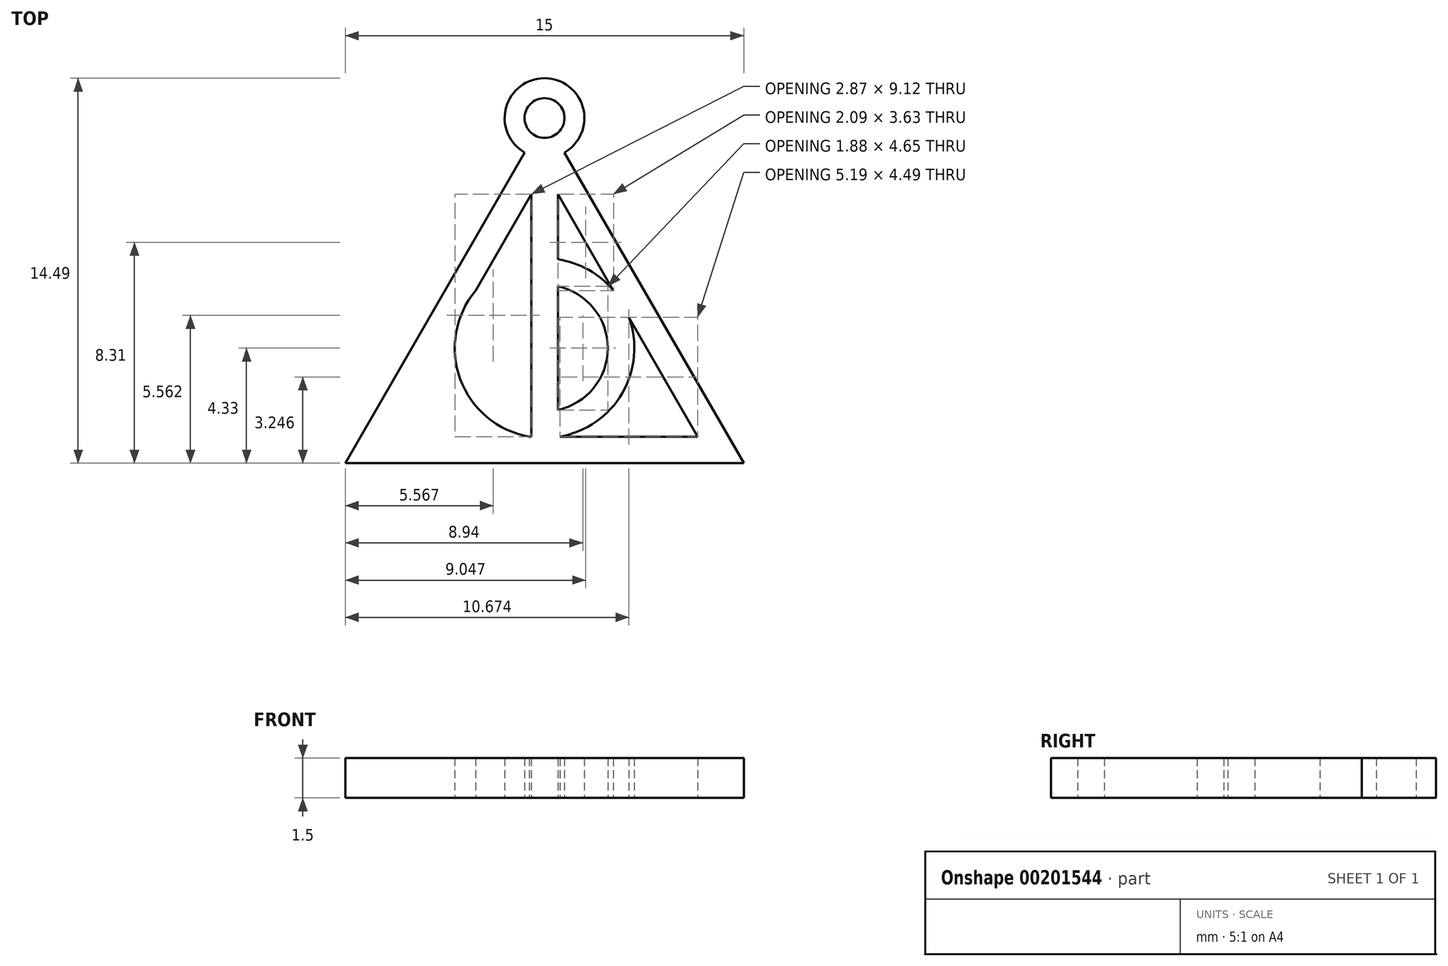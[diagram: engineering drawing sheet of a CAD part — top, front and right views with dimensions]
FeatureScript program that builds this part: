
annotation { "Feature Type Name" : "Feature", "Feature Type Description" : "" }
export const myFeature = defineFeature(function(context is Context, id is Id, definition is map)
    precondition{}
    {
        {
            var Q0;
            Q0=qCreatedBy(makeId("Top.planeOp"),FACE);
            var sketch = newSketch(context, id + "F0", { "sketchPlane" : qUnion([Q0])});
            skLineSegment(sketch, "E0", {"start": v(0, 0) * mm, "end": v(-7.5, -13) * mm});
            skLineSegment(sketch, "E1", {"start": v(-7.5, -13) * mm, "end": v(7.5, -13) * mm});
            skLineSegment(sketch, "E2", {"start": v(7.5, -13) * mm, "end": v(0, 0) * mm});
            skCircle(sketch, "E3", {"center": v(0, 0) * mm, "radius": 1.5 * mm});
            skCircle(sketch, "E4", {"center": v(0, 0) * mm, "radius": 0.75 * mm});
            skLineSegment(sketch, "E5.0", {"start": v(0, -2) * mm, "end": v(-5.77, -12) * mm});
            skLineSegment(sketch, "E5.1", {"start": v(5.77, -12) * mm, "end": v(0, -2) * mm});
            skLineSegment(sketch, "E5.2", {"start": v(-5.77, -12) * mm, "end": v(5.77, -12) * mm});
            skLineSegment(sketch, "E6", {"start": v(0, 0) * mm, "end": v(0, -13) * mm, "construction": true});
            skLineSegment(sketch, "E7", {"start": v(-0.5, -2.87) * mm, "end": v(-0.5, -12) * mm});
            skLineSegment(sketch, "E8.MirrorCS", {"start": v(0.5, -2.87) * mm, "end": v(0.5, -12) * mm});
            skCircle(sketch, "E9", {"center": v(0, -8.66) * mm, "radius": 3.38 * mm});
            skLineSegment(sketch, "E10", {"start": v(0, -8.66) * mm, "end": v(-2.93, -6.97) * mm, "construction": true});
            skPoint(sketch, "E11", {"position": v(0, -12.04) * mm});
            skCircle(sketch, "E12.0", {"center": v(0, -8.66) * mm, "radius": 2.38 * mm});
            skSolve(sketch);
        }
        {
            var Q0;
            {var subQ0=sQuery(id+"F0.wireOp",EDGE,"E3");var subQ1=sQuery(id+"F0.wireOp",EDGE,"E0");var subQ2=makeQuery(id+"F0.imprint","INTERSECT",VERTEX,{"derivedFrom":[subQ1,subQ0]});Q0=makeQuery(id+"F0.imprint","IMPRINT",FACE,{"disambiguationData":[TD([[makeQuery(id+"F0.imprint","IMPRINT",EDGE,{"disambiguationData":[TD([[subQ2,1.0]])],"derivedFrom":subQ1}),-1.0]])]});}
            var Q1;
            {var subQ0=sQuery(id+"F0.wireOp",EDGE,"E3");var subQ1=sQuery(id+"F0.wireOp",EDGE,"E0");var subQ2=makeQuery(id+"F0.imprint","INTERSECT",VERTEX,{"derivedFrom":[subQ1,subQ0]});Q1=makeQuery(id+"F0.imprint","IMPRINT",FACE,{"disambiguationData":[TD([[makeQuery(id+"F0.imprint","IMPRINT",EDGE,{"disambiguationData":[TD([[subQ2,1.0]])],"derivedFrom":subQ1}),1.0]])]});}
            var Q2;
            {var subQ1=sQuery(id+"F0.wireOp",EDGE,"E5.1");var subQ5=sQuery(id+"F0.wireOp",EDGE,"E5.0");var subQ6=makeQuery(id+"F0.imprint","INTERSECT",VERTEX,{"derivedFrom":[subQ5,subQ1]});Q2=makeQuery(id+"F0.imprint","IMPRINT",FACE,{"disambiguationData":[TD([[makeQuery(id+"F0.imprint","IMPRINT",EDGE,{"disambiguationData":[TD([[subQ6,-1.0]])],"derivedFrom":subQ5}),1.0]])]});}
            var Q3;
            {var subQ0=sQuery(id+"F0.wireOp",EDGE,"E12.0");var subQ1=sQuery(id+"F0.wireOp",EDGE,"E7");var subQ2=makeQuery(id+"F0.imprint","INTERSECT",VERTEX,{"disambiguationData":[OD(0.0)],"derivedFrom":[subQ1,subQ0]});Q3=makeQuery(id+"F0.imprint","IMPRINT",FACE,{"disambiguationData":[TD([[makeQuery(id+"F0.imprint","IMPRINT",EDGE,{"disambiguationData":[TD([[subQ2,-1.0]])],"derivedFrom":subQ1}),1.0]])]});}
            var Q4;
            {var subQ10=sQuery(id+"F0.wireOp",EDGE,"E1");Q4=makeQuery(id+"F0.imprint","IMPRINT",FACE,{"disambiguationData":[TD([[makeQuery(id+"F0.imprint","IMPRINT",EDGE,{"derivedFrom":subQ10}),1.0]])]});}
            var Q5;
            {var subQ0=sQuery(id+"F0.wireOp",EDGE,"E9");var subQ9=sQuery(id+"F0.wireOp",EDGE,"E5.0");var subQ10=makeQuery(id+"F0.imprint","INTERSECT",VERTEX,{"disambiguationData":[OD(0.0)],"derivedFrom":[subQ9,subQ0]});Q5=makeQuery(id+"F0.imprint","IMPRINT",FACE,{"disambiguationData":[TD([[makeQuery(id+"F0.imprint","IMPRINT",EDGE,{"disambiguationData":[TD([[subQ10,-1.0]])],"derivedFrom":subQ9}),1.0]])]});}
            var Q6;
            {var subQ5=sQuery(id+"F0.wireOp",EDGE,"E9");var subQ9=sQuery(id+"F0.wireOp",EDGE,"E5.1");var subQ11=makeQuery(id+"F0.imprint","INTERSECT",VERTEX,{"disambiguationData":[OD(0.0)],"derivedFrom":[subQ9,subQ5]});Q6=makeQuery(id+"F0.imprint","IMPRINT",FACE,{"disambiguationData":[TD([[makeQuery(id+"F0.imprint","IMPRINT",EDGE,{"disambiguationData":[TD([[subQ11,-1.0]])],"derivedFrom":subQ9}),1.0]])]});}
            var Q7;
            {var subQ0=sQuery(id+"F0.wireOp",EDGE,"E9");var subQ1=sQuery(id+"F0.wireOp",EDGE,"E7");var subQ2=makeQuery(id+"F0.imprint","INTERSECT",VERTEX,{"derivedFrom":[subQ1,subQ0]});Q7=makeQuery(id+"F0.imprint","IMPRINT",FACE,{"disambiguationData":[TD([[makeQuery(id+"F0.imprint","IMPRINT",EDGE,{"disambiguationData":[TD([[subQ2,-1.0]])],"derivedFrom":subQ1}),1.0]])]});}
            var Q8;
            {var subQ0=sQuery(id+"F0.wireOp",EDGE,"E7");var subQ1=sQuery(id+"F0.wireOp",EDGE,"E5.2");var subQ2=makeQuery(id+"F0.imprint","INTERSECT",VERTEX,{"derivedFrom":[subQ1,subQ0]});Q8=makeQuery(id+"F0.imprint","IMPRINT",FACE,{"disambiguationData":[TD([[makeQuery(id+"F0.imprint","IMPRINT",EDGE,{"disambiguationData":[TD([[subQ2,-1.0]])],"derivedFrom":subQ1}),1.0]])]});}
            var Q9;
            {var subQ0=sQuery(id+"F0.wireOp",EDGE,"E5.2");var subQ1=makeQuery(id+"F0.imprint","INTERSECT",VERTEX,{"derivedFrom":[subQ0,sQuery(id+"F0.wireOp",EDGE,"E7")]});Q9=makeQuery(id+"F0.imprint","IMPRINT",FACE,{"disambiguationData":[TD([[makeQuery(id+"F0.imprint","IMPRINT",EDGE,{"disambiguationData":[TD([[subQ1,1.0]])],"derivedFrom":subQ0}),-1.0]])]});}
            var Q10;
            {var subQ0=sQuery(id+"F0.wireOp",EDGE,"E9");var subQ1=sQuery(id+"F0.wireOp",EDGE,"E5.0");var subQ2=makeQuery(id+"F0.imprint","INTERSECT",VERTEX,{"disambiguationData":[OD(0.0)],"derivedFrom":[subQ1,subQ0]});Q10=makeQuery(id+"F0.imprint","IMPRINT",FACE,{"disambiguationData":[TD([[makeQuery(id+"F0.imprint","IMPRINT",EDGE,{"disambiguationData":[TD([[subQ2,-1.0]])],"derivedFrom":subQ1}),-1.0]])]});}
            var Q11;
            {var subQ0=sQuery(id+"F0.wireOp",EDGE,"E9");var subQ1=sQuery(id+"F0.wireOp",EDGE,"E5.1");var subQ2=makeQuery(id+"F0.imprint","INTERSECT",VERTEX,{"disambiguationData":[OD(0.0)],"derivedFrom":[subQ1,subQ0]});Q11=makeQuery(id+"F0.imprint","IMPRINT",FACE,{"disambiguationData":[TD([[makeQuery(id+"F0.imprint","IMPRINT",EDGE,{"disambiguationData":[TD([[subQ2,-1.0]])],"derivedFrom":subQ1}),-1.0]])]});}
            extrude(context, id + "F1", {"entities" : qUnion([Q0, Q1, Q2, Q3, Q4, Q5, Q6, Q7, Q8, Q9, Q10, Q11]), "depth" : 1.5 * mm});
        }
    });
